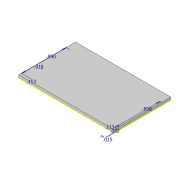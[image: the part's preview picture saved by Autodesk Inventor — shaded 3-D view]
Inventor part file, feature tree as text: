
AUTODESK INVENTOR PART (.ipt)
format: ipt  version: 2018.3 (Build 223284000, 284)  size: 84,992 bytes
history: native  units: in
note: dims shown in document units (in); Inventor stores cm internally (conversion verified against a paired STEP export)
features: sketch x2, extrude x1
ambient origin geometry x8: Origin, YZ Plane, XZ Plane, XY Plane, X Axis, Y Axis, Z Axis, Center Point
bodies: Solid1 (feature_tree)
feature tree (3):
  extrude  "Extrusion1"  Depth=1.125in
  sketch  "Sketch2"  dims[d2=0.0625in d3=0.0in d4=0.89in d5=0.89in d6=0.1125in d7=0.1125in d8=0.0151in d9=0.0156in d10=0.0323in]
  sketch  "Sketch1"  dims[d0=1.887in d1=1.125in]
